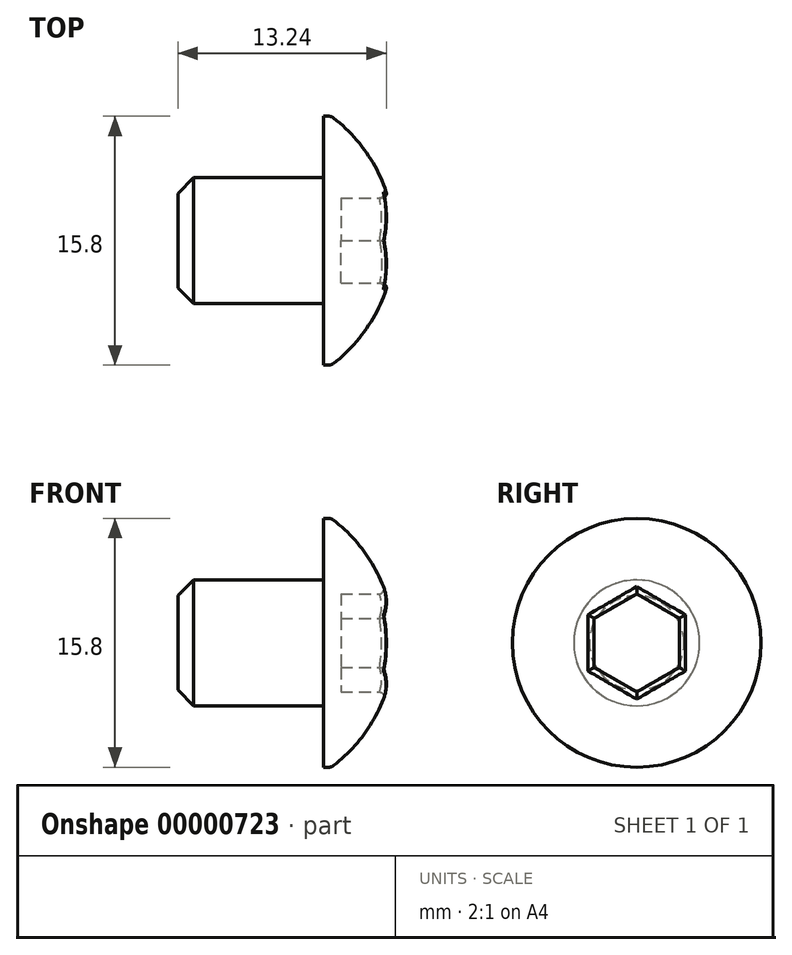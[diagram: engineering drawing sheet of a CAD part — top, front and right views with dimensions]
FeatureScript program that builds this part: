
annotation { "Feature Type Name" : "Feature", "Feature Type Description" : "" }
export const myFeature = defineFeature(function(context is Context, id is Id, definition is map)
    precondition{}
    {
        {
            var Q0;
            Q0=qCreatedBy(makeId("Front.planeOp"),FACE);
            var sketch = newSketch(context, id + "F0", { "sketchPlane" : qUnion([Q0])});
            skLineSegment(sketch, "E0", {"start": v(0, 4) * mm, "end": v(0, 7.9) * mm});
            skLineSegment(sketch, "E1", {"start": v(0, 7.9) * mm, "end": v(0.5, 7.9) * mm});
            skLineSegment(sketch, "E2", {"start": v(0, 4) * mm, "end": v(-9.25, 4) * mm});
            skLineSegment(sketch, "E3", {"start": v(-9.25, 4) * mm, "end": v(-9.25, 0) * mm});
            skLineSegment(sketch, "E4", {"start": v(-9.25, 0) * mm, "end": v(4.5, 0) * mm});
            skArc(sketch, "E5", {"start": v(4.5, 0) * mm, "mid": v(3.42, 4.42) * mm, "end": v(0.5, 7.9) * mm});
            skLineSegment(sketch, "E6", {"start": v(-9.25, 0) * mm, "end": v(-45.57, 0) * mm, "construction": true});
            skSolve(sketch);
        }
        {
            var Q0;
            Q0=makeQuery(id+"F0.imprint","IMPRINT",FACE,{"disambiguationData":[TD([[makeQuery(id+"F0.imprint","IMPRINT",EDGE,{"derivedFrom":sQuery(id+"F0.wireOp",EDGE,"E0")}),-1.0]])]});
            var Q1;
            Q1=sQuery(id+"F0.wireOp",EDGE,"E6");
            revolve(context, id + "F1", {"entities" : qUnion([Q0]), "axis" : qUnion([Q1]), "revolveType" : RevolveType.FULL});
        }
        {
            var Q0;
            Q0=makeQuery(id+"F1.opRevolve","SWEPT_EDGE",EDGE,{"disambiguationData":[OSD([sQuery(id+"F0.wireOp",EDGE,"E2"),sQuery(id+"F0.wireOp",EDGE,"E3")])]});
            chamfer(context, id + "F2", {"entities" : qUnion([Q0]), "width" : 1 * mm, "tangentPropagation" : true});
        }
        {
            var Q0;
            Q0=makeQuery(id+"F1.opRevolve","SWEPT_EDGE",EDGE,{"disambiguationData":[OSD([sQuery(id+"F0.wireOp",EDGE,"E1"),sQuery(id+"F0.wireOp",EDGE,"E5")])]});
            fillet(context, id + "F3", {"entities" : qUnion([Q0]), "radius" : .5 * mm, "tangentPropagation" : true, "allowEdgeOverflow" : false});
        }
        {
            var Q0;
            Q0=qCreatedBy(makeId("Right.planeOp"),FACE);
            cPlane(context, id + "F4", {"entities" : qUnion([Q0]), "cplaneType" : CPlaneType.OFFSET, "offset" : 4.5 * mm, "width" : 150 * mm, "height" : 150 * mm});
        }
        {
            var Q0;
            Q0=qCreatedBy(id+"F4.planeOp",FACE);
            var sketch = newSketch(context, id + "F5", { "sketchPlane" : qUnion([Q0])});
            skCircle(sketch, "E7.cCircle", {"center": v(0, 0) * mm, "radius": 2.7 * mm, "construction": true});
            skLineSegment(sketch, "E7.0", {"start": v(2.7, -1.56) * mm, "end": v(0, -3.12) * mm});
            skLineSegment(sketch, "E7.1", {"start": v(0, -3.12) * mm, "end": v(-2.7, -1.56) * mm});
            skLineSegment(sketch, "E7.2", {"start": v(-2.7, -1.56) * mm, "end": v(-2.7, 1.56) * mm});
            skLineSegment(sketch, "E7.3", {"start": v(-2.7, 1.56) * mm, "end": v(0, 3.12) * mm});
            skLineSegment(sketch, "E7.4", {"start": v(0, 3.12) * mm, "end": v(2.7, 1.56) * mm});
            skLineSegment(sketch, "E7.5", {"start": v(2.7, 1.56) * mm, "end": v(2.7, -1.56) * mm});
            skPoint(sketch, "E7.0.midPoint", {"position": v(1.35, -2.34) * mm});
            skSolve(sketch);
        }
        {
            var Q0;
            Q0=makeQuery(id+"F5.imprint","IMPRINT",FACE,{"disambiguationData":[TD([[makeQuery(id+"F5.imprint","IMPRINT",EDGE,{"derivedFrom":sQuery(id+"F5.wireOp",EDGE,"E7.0")}),-1.0]])]});
            extrude(context, id + "F6", {"entities" : qUnion([Q0]), "operationType" : NewBodyOperationType.REMOVE, "oppositeDirection" : true, "depth" : 3.4 * mm});
        }
        {
            var Q0;
            Q0=makeQuery(id+"F6.boolean.opBoolean","INTERSECT",EDGE,{"derivedFrom":[makeQuery(id+"F1.opRevolve","SWEPT_FACE",FACE,{"disambiguationData":[OSD([sQuery(id+"F0.wireOp",EDGE,"E5")])]}),makeQuery(id+"F6.opExtrude","SWEPT_FACE",FACE,{"disambiguationData":[OSD([sQuery(id+"F5.wireOp",EDGE,"E7.2")])]})]});
            var Q1;
            Q1=makeQuery(id+"F6.boolean.opBoolean","INTERSECT",EDGE,{"derivedFrom":[makeQuery(id+"F1.opRevolve","SWEPT_FACE",FACE,{"disambiguationData":[OSD([sQuery(id+"F0.wireOp",EDGE,"E5")])]}),makeQuery(id+"F6.opExtrude","SWEPT_FACE",FACE,{"disambiguationData":[OSD([sQuery(id+"F5.wireOp",EDGE,"E7.1")])]})]});
            var Q2;
            Q2=makeQuery(id+"F6.boolean.opBoolean","INTERSECT",EDGE,{"derivedFrom":[makeQuery(id+"F1.opRevolve","SWEPT_FACE",FACE,{"disambiguationData":[OSD([sQuery(id+"F0.wireOp",EDGE,"E5")])]}),makeQuery(id+"F6.opExtrude","SWEPT_FACE",FACE,{"disambiguationData":[OSD([sQuery(id+"F5.wireOp",EDGE,"E7.0")])]})]});
            var Q3;
            Q3=makeQuery(id+"F6.boolean.opBoolean","INTERSECT",EDGE,{"derivedFrom":[makeQuery(id+"F1.opRevolve","SWEPT_FACE",FACE,{"disambiguationData":[OSD([sQuery(id+"F0.wireOp",EDGE,"E5")])]}),makeQuery(id+"F6.opExtrude","SWEPT_FACE",FACE,{"disambiguationData":[OSD([sQuery(id+"F5.wireOp",EDGE,"E7.5")])]})]});
            var Q4;
            Q4=makeQuery(id+"F6.boolean.opBoolean","INTERSECT",EDGE,{"derivedFrom":[makeQuery(id+"F1.opRevolve","SWEPT_FACE",FACE,{"disambiguationData":[OSD([sQuery(id+"F0.wireOp",EDGE,"E5")])]}),makeQuery(id+"F6.opExtrude","SWEPT_FACE",FACE,{"disambiguationData":[OSD([sQuery(id+"F5.wireOp",EDGE,"E7.4")])]})]});
            var Q5;
            Q5=makeQuery(id+"F6.boolean.opBoolean","INTERSECT",EDGE,{"derivedFrom":[makeQuery(id+"F1.opRevolve","SWEPT_FACE",FACE,{"disambiguationData":[OSD([sQuery(id+"F0.wireOp",EDGE,"E5")])]}),makeQuery(id+"F6.opExtrude","SWEPT_FACE",FACE,{"disambiguationData":[OSD([sQuery(id+"F5.wireOp",EDGE,"E7.3")])]})]});
            fillet(context, id + "F7", {"entities" : qUnion([Q0, Q1, Q2, Q3, Q4, Q5]), "radius" : .3 * mm, "tangentPropagation" : true, "allowEdgeOverflow" : false});
        }
    });
